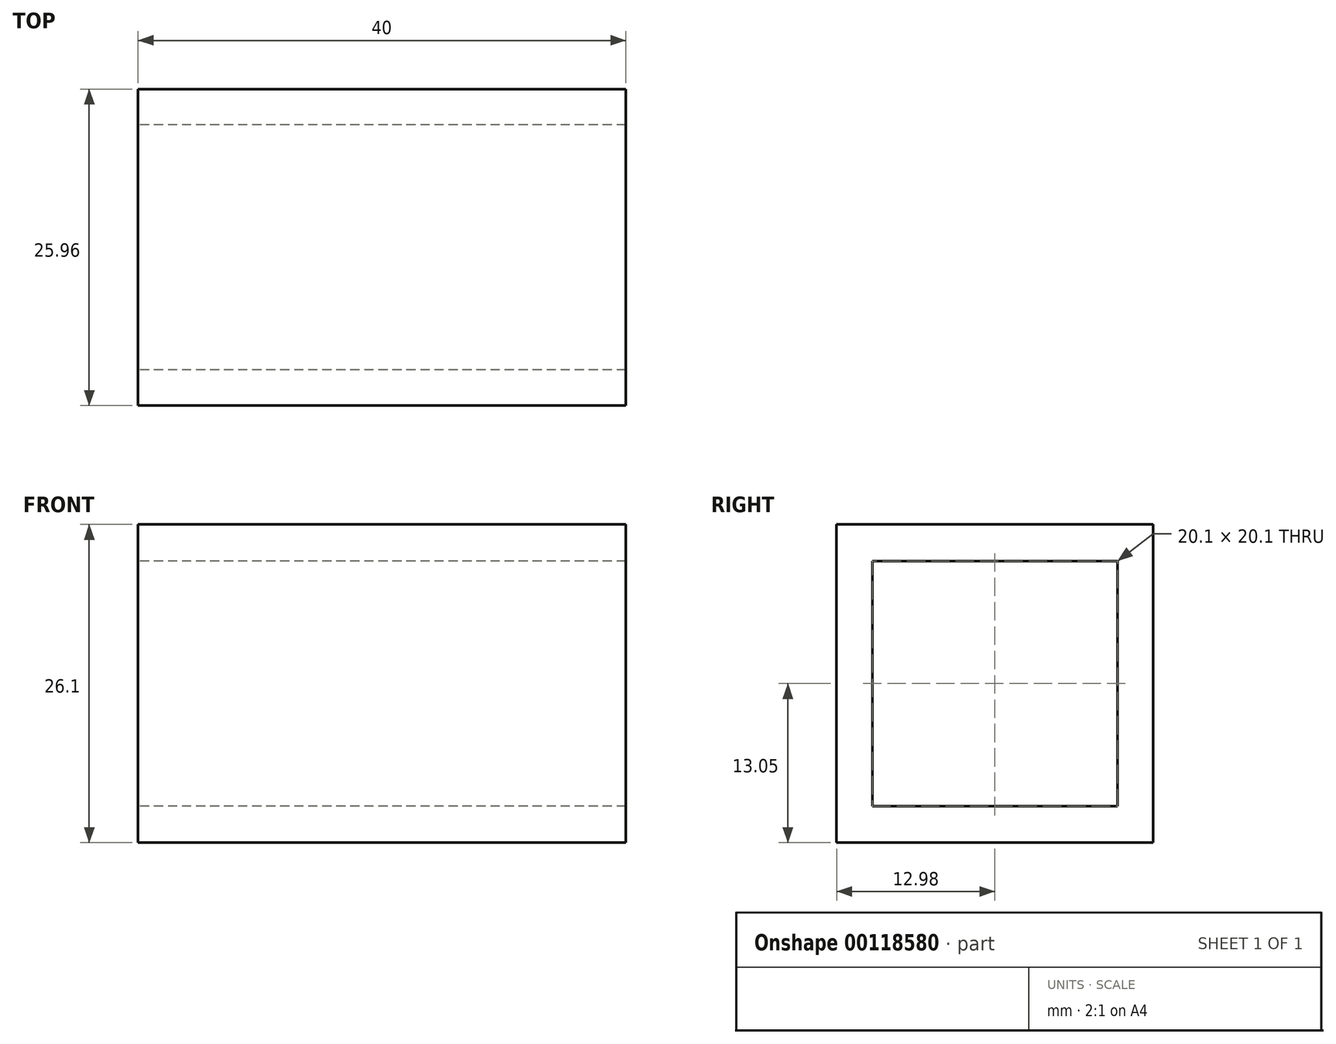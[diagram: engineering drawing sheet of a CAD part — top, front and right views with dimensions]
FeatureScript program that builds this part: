
annotation { "Feature Type Name" : "Feature", "Feature Type Description" : "" }
export const myFeature = defineFeature(function(context is Context, id is Id, definition is map)
    precondition{}
    {
        {
            var Q0;
            Q0=qCreatedBy(makeId("Right.planeOp"),FACE);
            var sketch = newSketch(context, id + "F0", { "sketchPlane" : qUnion([Q0])});
            skLineSegment(sketch, "E0.bottom", {"start": v(12.98, 13.05) * mm, "end": v(-12.98, 13.05) * mm});
            skLineSegment(sketch, "E0.top", {"start": v(12.98, -13.05) * mm, "end": v(-12.98, -13.05) * mm});
            skLineSegment(sketch, "E0.left", {"start": v(12.98, 13.05) * mm, "end": v(12.98, -13.05) * mm});
            skLineSegment(sketch, "E0.right", {"start": v(-12.98, 13.05) * mm, "end": v(-12.98, -13.05) * mm});
            skPoint(sketch, "E0.middle", {"position": v(0, 0) * mm});
            skLineSegment(sketch, "E1.bottom", {"start": v(10.05, 10.05) * mm, "end": v(-10.05, 10.05) * mm});
            skLineSegment(sketch, "E1.top", {"start": v(10.05, -10.05) * mm, "end": v(-10.05, -10.05) * mm});
            skLineSegment(sketch, "E1.left", {"start": v(10.05, 10.05) * mm, "end": v(10.05, -10.05) * mm});
            skLineSegment(sketch, "E1.right", {"start": v(-10.05, 10.05) * mm, "end": v(-10.05, -10.05) * mm});
            skSolve(sketch);
        }
        {
            var Q0;
            Q0 = qSketchRegion(id + "F0", true);
            extrude(context, id + "F1", {"entities" : qUnion([Q0]), "depth" : 40 * mm});
        }
    });
